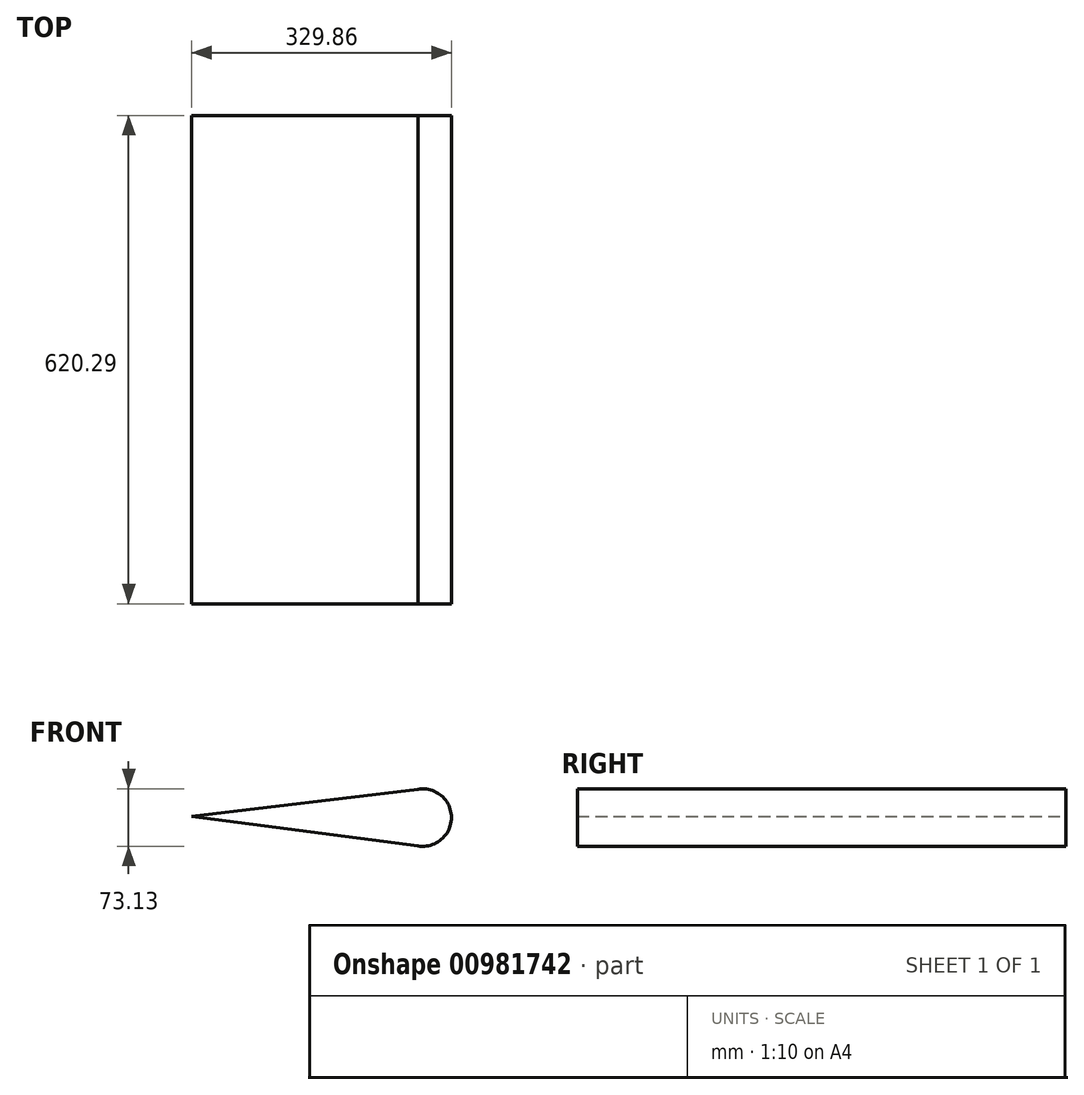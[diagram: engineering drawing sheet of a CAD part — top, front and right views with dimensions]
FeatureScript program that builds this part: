
annotation { "Feature Type Name" : "Feature", "Feature Type Description" : "" }
export const myFeature = defineFeature(function(context is Context, id is Id, definition is map)
    precondition{}
    {
        {
            var Q0;
            Q0=qCreatedBy(makeId("Front.planeOp"),FACE);
            var sketch = newSketch(context, id + "F0", { "sketchPlane" : qUnion([Q0])});
            skArc(sketch, "E0", {"start": v(0, -37.92) * mm, "mid": v(42.32, -1.8) * mm, "end": v(0, 34.3) * mm});
            skLineSegment(sketch, "E1", {"start": v(0, -37.92) * mm, "end": v(-287.54, 0) * mm});
            skLineSegment(sketch, "E2", {"start": v(-287.54, 0) * mm, "end": v(0, 34.3) * mm});
            skSolve(sketch);
        }
        {
            var Q0;
            Q0=makeQuery(id+"F0.imprint","IMPRINT",FACE,{"disambiguationData":[TD([[makeQuery(id+"F0.imprint","IMPRINT",EDGE,{"derivedFrom":sQuery(id+"F0.wireOp",EDGE,"E0")}),1.0]])]});
            extrude(context, id + "F1", {"entities" : qUnion([Q0]), "depth" : 620.3 * mm, "offsetDistance" : 25.4 * mm});
        }
        {
            var Q0;
            Q0=qCreatedBy(makeId("Front.planeOp"),FACE);
            var sketch = newSketch(context, id + "F2", { "sketchPlane" : qUnion([Q0])});
            skLineSegment(sketch, "E3", {"start": v(-283.1, 0) * mm, "end": v(-342.68, -38.71) * mm});
            skSolve(sketch);
        }
        {
            var Q0;
            Q0=sQuery(id+"F2.wireOp",EDGE,"E3");
            extrude(context, id + "F3", {"bodyType" : ToolBodyType.SURFACE, "surfaceEntities" : qUnion([Q0]), "depth" : 617.53 * mm, "offsetDistance" : 25.4 * mm});
        }
    });
